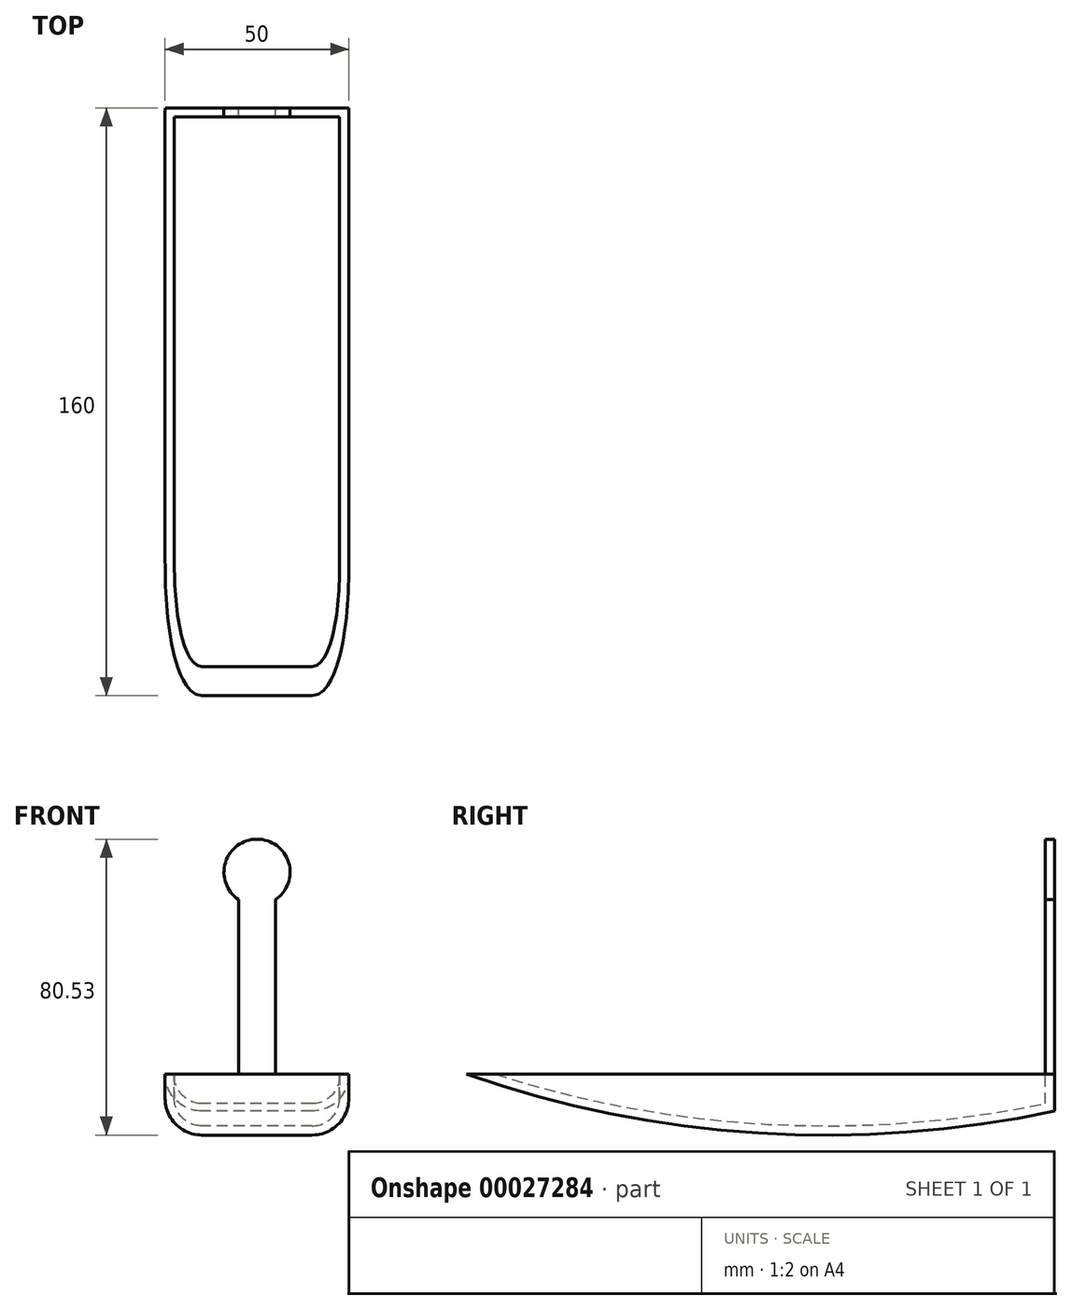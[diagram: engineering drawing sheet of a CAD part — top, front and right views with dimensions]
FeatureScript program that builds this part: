
annotation { "Feature Type Name" : "Feature", "Feature Type Description" : "" }
export const myFeature = defineFeature(function(context is Context, id is Id, definition is map)
    precondition{}
    {
        {
            var Q0;
            Q0=qCreatedBy(makeId("Right.planeOp"),FACE);
            var sketch = newSketch(context, id + "F0", { "sketchPlane" : qUnion([Q0])});
            skLineSegment(sketch, "E0", {"start": v(-80, 0) * mm, "end": v(80, 0) * mm});
            skArc(sketch, "E1", {"start": v(-80, 0) * mm, "mid": v(-0.68, -15.95) * mm, "end": v(80, -10) * mm});
            skLineSegment(sketch, "E2", {"start": v(80, -10) * mm, "end": v(80, 0) * mm});
            skSolve(sketch);
        }
        {
            var Q0;
            Q0 = qSketchRegion(id + "F0", true);
            extrude(context, id + "F1", {"entities" : qUnion([Q0]), "depth" : 25 * mm, "hasSecondDirection" : true, "secondDirectionOppositeDirection" : true, "secondDirectionDepth" : 25 * mm});
        }
        {
            var Q0;
            Q0=makeQuery(id+"F1.opExtrude","CAP_EDGE",EDGE,{"disambiguationData":[OSD([sQuery(id+"F0.wireOp",EDGE,"E1")])],"isStart":true});
            var Q1;
            Q1=makeQuery(id+"F1.opExtrude","CAP_EDGE",EDGE,{"disambiguationData":[OSD([sQuery(id+"F0.wireOp",EDGE,"E1")])],"isStart":false});
            fillet(context, id + "F2", {"entities" : qUnion([Q0, Q1]), "radius" : 10 * mm, "tangentPropagation" : true, "allowEdgeOverflow" : false});
        }
        {
            var Q0;
            Q0=makeQuery(id+"F1.opExtrude","SWEPT_FACE",FACE,{"disambiguationData":[OSD([sQuery(id+"F0.wireOp",EDGE,"E2")])]});
            var sketch = newSketch(context, id + "F3", { "sketchPlane" : qUnion([Q0])});
            skLineSegment(sketch, "E3", {"start": v(0, 0) * mm, "end": v(0, 46) * mm, "construction": true});
            skLineSegment(sketch, "E4", {"start": v(-5, 0) * mm, "end": v(-5, 47.52) * mm});
            skLineSegment(sketch, "E5", {"start": v(5, 0) * mm, "end": v(5, 47.52) * mm});
            skCircle(sketch, "E6", {"center": v(0, 55) * mm, "radius": 9 * mm});
            skSolve(sketch);
        }
        {
            var Q0;
            Q0=makeQuery(id+"F1.opExtrude","SWEPT_FACE",FACE,{"disambiguationData":[OSD([sQuery(id+"F0.wireOp",EDGE,"E0")])]});
            shell(context, id + "F4", {"entities" : qUnion([Q0]), "thickness" : 2.5 * mm});
        }
        {
            var Q0;
            {var subQ2=sQuery(id+"F3.wireOp",EDGE,"E4");Q0=makeQuery(id+"F3.imprint","IMPRINT",FACE,{"disambiguationData":[TD([[makeQuery(id+"F3.imprint","IMPRINT",EDGE,{"derivedFrom":subQ2}),-1.0]])]});}
            var Q1;
            {var subQ0=sQuery(id+"F3.wireOp",EDGE,"E6");var subQ2=makeQuery(id+"F3.imprint","INTERSECT",VERTEX,{"derivedFrom":[sQuery(id+"F3.wireOp",EDGE,"E4"),subQ0]});Q1=makeQuery(id+"F3.imprint","IMPRINT",FACE,{"disambiguationData":[TD([[makeQuery(id+"F3.imprint","IMPRINT",EDGE,{"disambiguationData":[TD([[subQ2,-1.0]])],"derivedFrom":subQ0}),1.0]])]});}
            var Q2;
            Q2=makeQuery(id+"F4.opShell","OFFSET_FACE",FACE,{"disambiguationData":[OSD([sQuery(id+"F0.wireOp",EDGE,"E2")])]});
            extrude(context, id + "F5", {"entities" : qUnion([Q0, Q1]), "operationType" : NewBodyOperationType.ADD, "endBound" : BoundingType.UP_TO_SURFACE, "oppositeDirection" : true, "endBoundEntityFace" : qUnion([Q2]), "depth" : 25 * mm});
        }
    });
